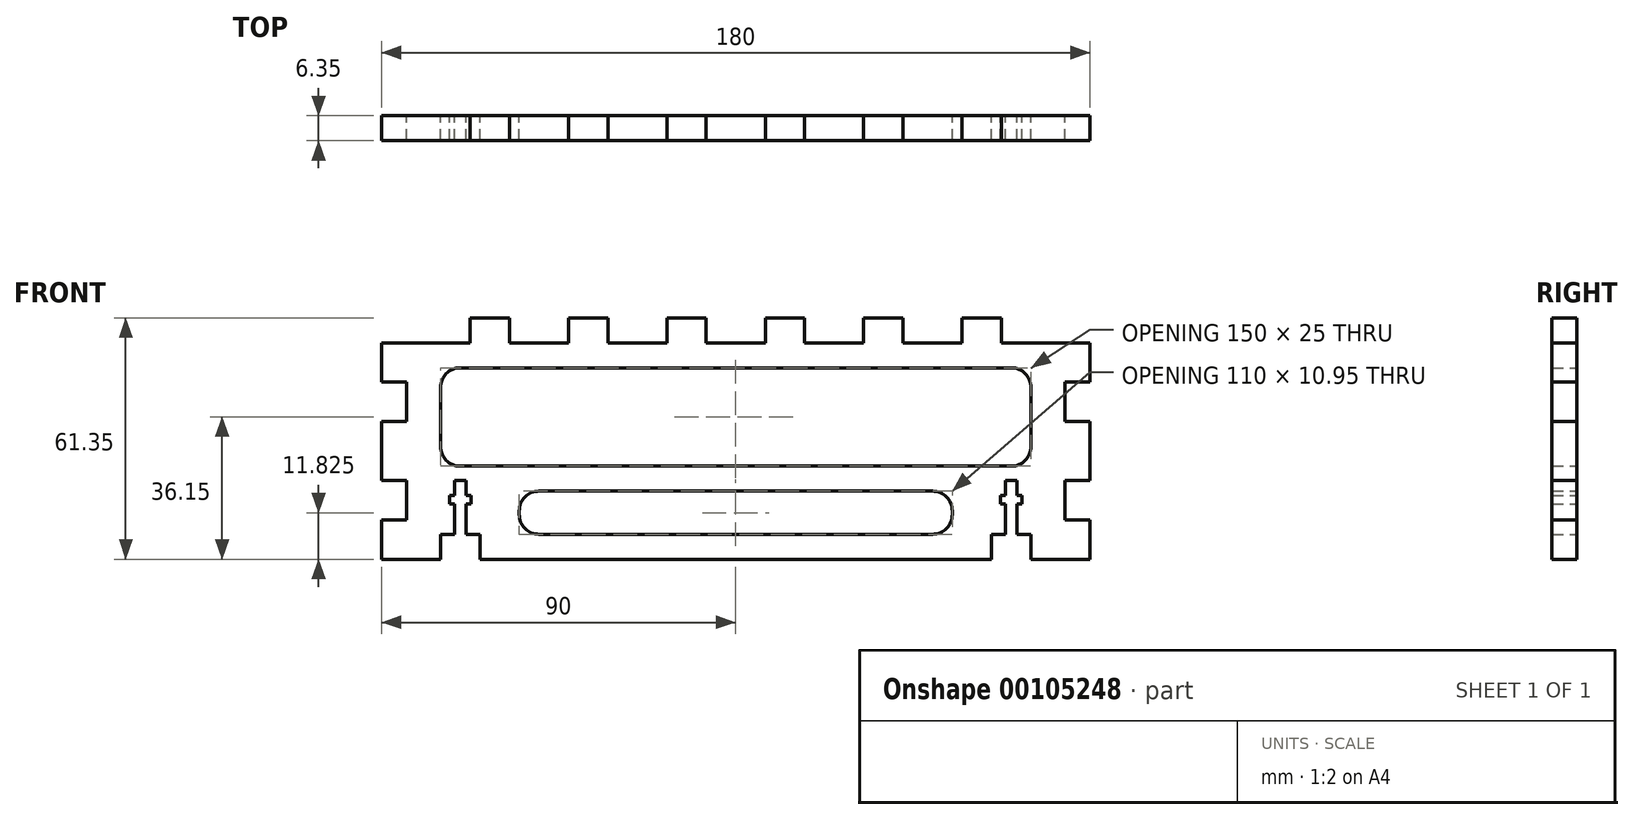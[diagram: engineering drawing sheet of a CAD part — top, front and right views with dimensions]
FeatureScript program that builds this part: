
annotation { "Feature Type Name" : "Feature", "Feature Type Description" : "" }
export const myFeature = defineFeature(function(context is Context, id is Id, definition is map)
    precondition{}
    {
        {
            var Q0;
            Q0=qCreatedBy(makeId("Front.planeOp"),FACE);
            var sketch = newSketch(context, id + "F0", { "sketchPlane" : qUnion([Q0])});
            skLineSegment(sketch, "E0.bottom", {"start": v(0, 0) * mm, "end": v(15, 0) * mm});
            skLineSegment(sketch, "E0.left", {"start": v(0, 0) * mm, "end": v(0, 10) * mm});
            skLineSegment(sketch, "E0.right", {"start": v(180, 0) * mm, "end": v(180, 10) * mm});
            skLineSegment(sketch, "E1.top", {"start": v(22.5, 61.35) * mm, "end": v(32.5, 61.35) * mm});
            skLineSegment(sketch, "E1.left", {"start": v(22.5, 55) * mm, "end": v(22.5, 61.35) * mm});
            skLineSegment(sketch, "E1.right", {"start": v(32.5, 55) * mm, "end": v(32.5, 61.35) * mm});
            skLineSegment(sketch, "E2.1.0.0", {"start": v(57.5, 55) * mm, "end": v(57.5, 61.35) * mm});
            skLineSegment(sketch, "E2.1.0.1", {"start": v(47.5, 61.35) * mm, "end": v(57.5, 61.35) * mm});
            skLineSegment(sketch, "E2.1.0.3", {"start": v(47.5, 55) * mm, "end": v(47.5, 61.35) * mm});
            skLineSegment(sketch, "E2.2.0.0", {"start": v(82.5, 55) * mm, "end": v(82.5, 61.35) * mm});
            skLineSegment(sketch, "E2.2.0.1", {"start": v(72.5, 61.35) * mm, "end": v(82.5, 61.35) * mm});
            skLineSegment(sketch, "E2.2.0.3", {"start": v(72.5, 55) * mm, "end": v(72.5, 61.35) * mm});
            skLineSegment(sketch, "E2.3.0.0", {"start": v(107.5, 55) * mm, "end": v(107.5, 61.35) * mm});
            skLineSegment(sketch, "E2.3.0.1", {"start": v(97.5, 61.35) * mm, "end": v(107.5, 61.35) * mm});
            skLineSegment(sketch, "E2.3.0.3", {"start": v(97.5, 55) * mm, "end": v(97.5, 61.35) * mm});
            skLineSegment(sketch, "E2.4.0.0", {"start": v(132.5, 55) * mm, "end": v(132.5, 61.35) * mm});
            skLineSegment(sketch, "E2.4.0.1", {"start": v(122.5, 61.35) * mm, "end": v(132.5, 61.35) * mm});
            skLineSegment(sketch, "E2.4.0.3", {"start": v(122.5, 55) * mm, "end": v(122.5, 61.35) * mm});
            skLineSegment(sketch, "E2.5.0.0", {"start": v(157.5, 55) * mm, "end": v(157.5, 61.35) * mm});
            skLineSegment(sketch, "E2.5.0.1", {"start": v(147.5, 61.35) * mm, "end": v(157.5, 61.35) * mm});
            skLineSegment(sketch, "E2.5.0.3", {"start": v(147.5, 55) * mm, "end": v(147.5, 61.35) * mm});
            skLineSegment(sketch, "E2.direction1", {"start": v(22.5, 55) * mm, "end": v(47.5, 55) * mm, "construction": true});
            skLineSegment(sketch, "E3.trimOffspring", {"start": v(57.5, 55) * mm, "end": v(72.5, 55) * mm});
            skLineSegment(sketch, "E4.trimOffspring", {"start": v(82.5, 55) * mm, "end": v(97.5, 55) * mm});
            skLineSegment(sketch, "E5.trimOffspring", {"start": v(107.5, 55) * mm, "end": v(122.5, 55) * mm});
            skLineSegment(sketch, "E6.trimOffspring", {"start": v(157.5, 55) * mm, "end": v(180, 55) * mm});
            skLineSegment(sketch, "E7.trimOffspring", {"start": v(132.5, 55) * mm, "end": v(147.5, 55) * mm});
            skLineSegment(sketch, "E8", {"start": v(0, 55) * mm, "end": v(22.5, 55) * mm});
            skLineSegment(sketch, "E9", {"start": v(32.5, 55) * mm, "end": v(47.5, 55) * mm});
            skLineSegment(sketch, "E10.trimOffspring", {"start": v(25, 0) * mm, "end": v(155, 0) * mm});
            skLineSegment(sketch, "E11.trimOffspring", {"start": v(165, 0) * mm, "end": v(180, 0) * mm});
            skLineSegment(sketch, "E12.bottom", {"start": v(0, 45) * mm, "end": v(6.35, 45) * mm});
            skLineSegment(sketch, "E12.top", {"start": v(0, 35) * mm, "end": v(6.35, 35) * mm});
            skLineSegment(sketch, "E12.right", {"start": v(6.35, 45) * mm, "end": v(6.35, 35) * mm});
            skLineSegment(sketch, "E13.bottom", {"start": v(0, 20) * mm, "end": v(6.35, 20) * mm});
            skLineSegment(sketch, "E13.top", {"start": v(0, 10) * mm, "end": v(6.35, 10) * mm});
            skLineSegment(sketch, "E13.right", {"start": v(6.35, 20) * mm, "end": v(6.35, 10) * mm});
            skLineSegment(sketch, "E14.trimOffspring", {"start": v(0, 45) * mm, "end": v(0, 55) * mm});
            skLineSegment(sketch, "E15.trimOffspring", {"start": v(0, 20) * mm, "end": v(0, 35) * mm});
            skLineSegment(sketch, "E16.bottom", {"start": v(180, 45) * mm, "end": v(173.65, 45) * mm});
            skLineSegment(sketch, "E16.top", {"start": v(180, 35) * mm, "end": v(173.65, 35) * mm});
            skLineSegment(sketch, "E16.right", {"start": v(173.65, 45) * mm, "end": v(173.65, 35) * mm});
            skLineSegment(sketch, "E17.bottom", {"start": v(180, 20) * mm, "end": v(173.65, 20) * mm});
            skLineSegment(sketch, "E17.top", {"start": v(180, 10) * mm, "end": v(173.65, 10) * mm});
            skLineSegment(sketch, "E17.right", {"start": v(173.65, 20) * mm, "end": v(173.65, 10) * mm});
            skLineSegment(sketch, "E18.trimOffspring", {"start": v(180, 45) * mm, "end": v(180, 55) * mm});
            skLineSegment(sketch, "E19.trimOffspring", {"start": v(180, 20) * mm, "end": v(180, 35) * mm});
            skLineSegment(sketch, "E20.MirrorCS", {"start": v(21.5, 6.35) * mm, "end": v(21.5, 14) * mm});
            skLineSegment(sketch, "E21.MirrorCS", {"start": v(18.5, 6.35) * mm, "end": v(18.5, 14) * mm});
            skLineSegment(sketch, "E22.MirrorCS", {"start": v(18.5, 20) * mm, "end": v(21.5, 20) * mm});
            skLineSegment(sketch, "E23.bottom", {"start": v(17.3, 16.27) * mm, "end": v(18.5, 16.27) * mm});
            skLineSegment(sketch, "E23.top", {"start": v(17.3, 14) * mm, "end": v(18.5, 14) * mm});
            skLineSegment(sketch, "E23.left", {"start": v(17.3, 16.27) * mm, "end": v(17.3, 14) * mm});
            skLineSegment(sketch, "E23.right", {"start": v(22.7, 16.27) * mm, "end": v(22.7, 14) * mm});
            skLineSegment(sketch, "E24.trimOffspring", {"start": v(21.5, 16.27) * mm, "end": v(21.5, 20) * mm});
            skLineSegment(sketch, "E25.trimOffspring", {"start": v(18.5, 16.27) * mm, "end": v(18.5, 20) * mm});
            skLineSegment(sketch, "E26.trimOffspring", {"start": v(21.5, 16.27) * mm, "end": v(22.7, 16.27) * mm});
            skLineSegment(sketch, "E27.trimOffspring", {"start": v(21.5, 14) * mm, "end": v(22.7, 14) * mm});
            skLineSegment(sketch, "E28.top", {"start": v(25, 6.35) * mm, "end": v(21.5, 6.35) * mm});
            skLineSegment(sketch, "E28.left", {"start": v(25, 0) * mm, "end": v(25, 6.35) * mm});
            skLineSegment(sketch, "E29.top", {"start": v(18.5, 6.35) * mm, "end": v(15, 6.35) * mm});
            skLineSegment(sketch, "E29.right", {"start": v(15, 0) * mm, "end": v(15, 6.35) * mm});
            skPoint(sketch, "E30.orphan", {"position": v(21.5, 0) * mm});
            skPoint(sketch, "E31.orphan", {"position": v(18.5, 0) * mm});
            skLineSegment(sketch, "E32", {"start": v(90, 55) * mm, "end": v(90, 0) * mm, "construction": true});
            skLineSegment(sketch, "E33.MirrorCS", {"start": v(161.5, 20) * mm, "end": v(158.5, 20) * mm});
            skLineSegment(sketch, "E34.MirrorCS", {"start": v(162.7, 14) * mm, "end": v(161.5, 14) * mm});
            skLineSegment(sketch, "E35.MirrorCS", {"start": v(162.7, 16.27) * mm, "end": v(161.5, 16.27) * mm});
            skLineSegment(sketch, "E36.MirrorCS", {"start": v(158.5, 16.27) * mm, "end": v(158.5, 20) * mm});
            skLineSegment(sketch, "E37.MirrorCS", {"start": v(158.5, 6.35) * mm, "end": v(158.5, 14) * mm});
            skLineSegment(sketch, "E38.MirrorCS", {"start": v(161.5, 16.27) * mm, "end": v(161.5, 20) * mm});
            skLineSegment(sketch, "E39.MirrorCS", {"start": v(161.5, 6.35) * mm, "end": v(161.5, 14) * mm});
            skLineSegment(sketch, "E40.MirrorCS", {"start": v(161.5, 6.35) * mm, "end": v(165, 6.35) * mm});
            skLineSegment(sketch, "E41.MirrorCS", {"start": v(158.5, 16.27) * mm, "end": v(157.3, 16.27) * mm});
            skLineSegment(sketch, "E42.MirrorCS", {"start": v(157.3, 16.27) * mm, "end": v(157.3, 14) * mm});
            skLineSegment(sketch, "E43.MirrorCS", {"start": v(155, 6.35) * mm, "end": v(158.5, 6.35) * mm});
            skLineSegment(sketch, "E44.MirrorCS", {"start": v(155, 0) * mm, "end": v(155, 6.35) * mm});
            skLineSegment(sketch, "E45.MirrorCS", {"start": v(165, 0) * mm, "end": v(165, 6.35) * mm});
            skLineSegment(sketch, "E46.MirrorCS", {"start": v(162.7, 16.27) * mm, "end": v(162.7, 14) * mm});
            skLineSegment(sketch, "E47.MirrorCS", {"start": v(158.5, 14) * mm, "end": v(157.3, 14) * mm});
            skLineSegment(sketch, "E48.bottom", {"start": v(20, 48.65) * mm, "end": v(160, 48.65) * mm});
            skLineSegment(sketch, "E48.top", {"start": v(20, 23.65) * mm, "end": v(160, 23.65) * mm});
            skLineSegment(sketch, "E48.left", {"start": v(15, 43.65) * mm, "end": v(15, 28.65) * mm});
            skLineSegment(sketch, "E48.right", {"start": v(165, 43.65) * mm, "end": v(165, 28.65) * mm});
            skLineSegment(sketch, "E49.bottom", {"start": v(40, 17.3) * mm, "end": v(140, 17.3) * mm});
            skLineSegment(sketch, "E49.top", {"start": v(40, 6.35) * mm, "end": v(140, 6.35) * mm});
            skLineSegment(sketch, "E49.left", {"start": v(35, 12.3) * mm, "end": v(35, 11.35) * mm});
            skLineSegment(sketch, "E49.right", {"start": v(145, 12.3) * mm, "end": v(145, 11.35) * mm});
            skPoint(sketch, "E50.visualSharp", {"position": v(15, 48.65) * mm});
            skArc(sketch, "E50.filletArc", {"start": v(20, 48.65) * mm, "mid": v(16.46, 47.19) * mm, "end": v(15, 43.65) * mm});
            skPoint(sketch, "E51.visualSharp", {"position": v(165, 48.65) * mm});
            skArc(sketch, "E51.filletArc", {"start": v(165, 43.65) * mm, "mid": v(163.54, 47.19) * mm, "end": v(160, 48.65) * mm});
            skPoint(sketch, "E52.visualSharp", {"position": v(15, 23.65) * mm});
            skArc(sketch, "E52.filletArc", {"start": v(15, 28.65) * mm, "mid": v(16.46, 25.11) * mm, "end": v(20, 23.65) * mm});
            skPoint(sketch, "E53.visualSharp", {"position": v(165, 23.65) * mm});
            skArc(sketch, "E53.filletArc", {"start": v(160, 23.65) * mm, "mid": v(163.54, 25.11) * mm, "end": v(165, 28.65) * mm});
            skPoint(sketch, "E54.visualSharp", {"position": v(35, 17.3) * mm});
            skArc(sketch, "E54.filletArc", {"start": v(40, 17.3) * mm, "mid": v(36.46, 15.84) * mm, "end": v(35, 12.3) * mm});
            skPoint(sketch, "E55.visualSharp", {"position": v(35, 6.35) * mm});
            skArc(sketch, "E55.filletArc", {"start": v(35, 11.35) * mm, "mid": v(36.46, 7.81) * mm, "end": v(40, 6.35) * mm});
            skPoint(sketch, "E56.visualSharp", {"position": v(145, 6.35) * mm});
            skArc(sketch, "E56.filletArc", {"start": v(140, 6.35) * mm, "mid": v(143.54, 7.81) * mm, "end": v(145, 11.35) * mm});
            skPoint(sketch, "E57.visualSharp", {"position": v(145, 17.3) * mm});
            skArc(sketch, "E57.filletArc", {"start": v(145, 12.3) * mm, "mid": v(143.54, 15.84) * mm, "end": v(140, 17.3) * mm});
            skSolve(sketch);
        }
        {
            var Q0;
            Q0 = qSketchRegion(id + "F0", true);
            extrude(context, id + "F1", {"entities" : qUnion([Q0]), "depth" : 6.35 * mm});
        }
    });
